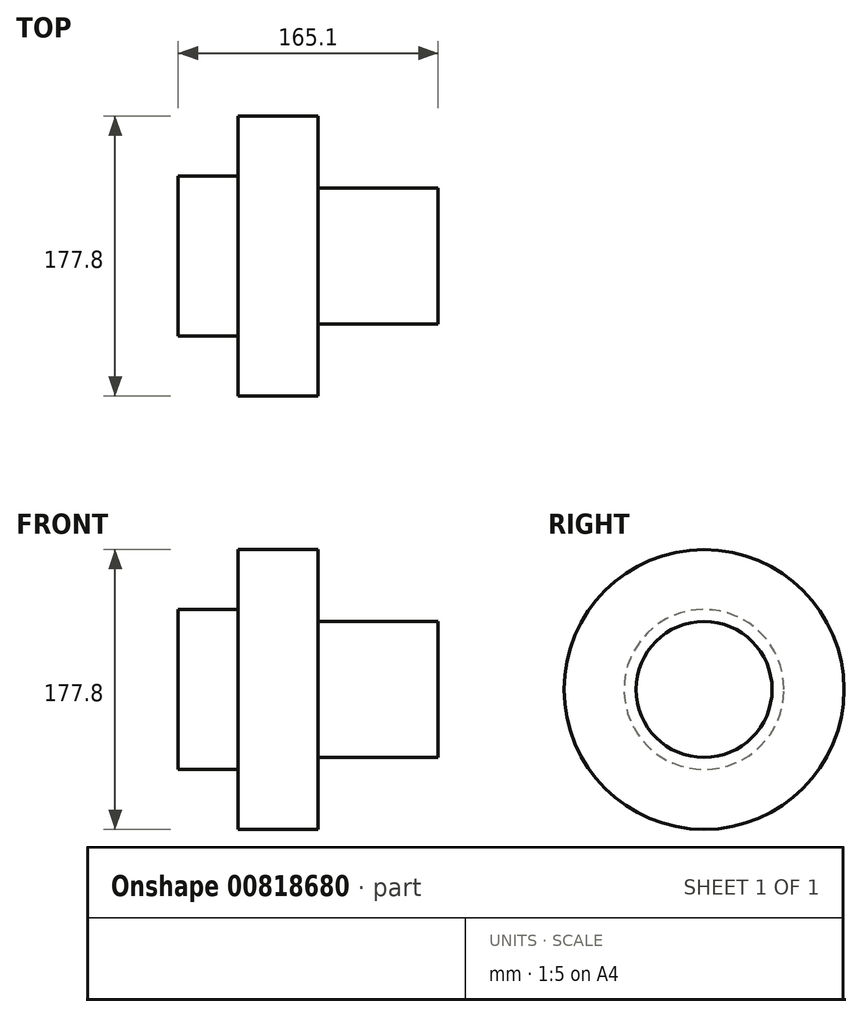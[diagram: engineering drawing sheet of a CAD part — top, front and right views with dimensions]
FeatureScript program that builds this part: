
annotation { "Feature Type Name" : "Feature", "Feature Type Description" : "" }
export const myFeature = defineFeature(function(context is Context, id is Id, definition is map)
    precondition{}
    {
        {
            var Q0;
            Q0=qCreatedBy(makeId("Front.planeOp"),FACE);
            var sketch = newSketch(context, id + "F0", { "sketchPlane" : qUnion([Q0])});
            skLineSegment(sketch, "E0", {"start": v(-70.84, 50.8) * mm, "end": v(-32.74, 50.8) * mm});
            skLineSegment(sketch, "E1", {"start": v(-32.74, 50.8) * mm, "end": v(-32.74, 88.9) * mm});
            skLineSegment(sketch, "E2", {"start": v(-32.74, 88.9) * mm, "end": v(18.06, 88.9) * mm});
            skLineSegment(sketch, "E3", {"start": v(18.06, 88.9) * mm, "end": v(18.06, 43.18) * mm});
            skLineSegment(sketch, "E4", {"start": v(18.06, 43.18) * mm, "end": v(94.26, 43.18) * mm});
            skLineSegment(sketch, "E5", {"start": v(94.26, 43.18) * mm, "end": v(94.26, 0) * mm});
            skLineSegment(sketch, "E6", {"start": v(94.26, 0) * mm, "end": v(-70.84, 0) * mm});
            skLineSegment(sketch, "E7", {"start": v(-70.84, 0) * mm, "end": v(-70.84, 50.8) * mm});
            skLineSegment(sketch, "E8", {"start": v(-139.12, 0) * mm, "end": v(143.44, 0) * mm, "construction": true});
            skSolve(sketch);
        }
        {
            var Q0;
            Q0=makeQuery(id+"F0.imprint","IMPRINT",FACE,{"disambiguationData":[TD([[makeQuery(id+"F0.imprint","IMPRINT",EDGE,{"derivedFrom":sQuery(id+"F0.wireOp",EDGE,"E0")}),-1.0]])]});
            var Q1;
            Q1=sQuery(id+"F0.wireOp",EDGE,"E8");
            revolve(context, id + "F1", {"surfaceOperationType" : NewSurfaceOperationType.NEW, "entities" : qUnion([Q0]), "axis" : qUnion([Q1]), "revolveType" : RevolveType.FULL});
        }
    });
